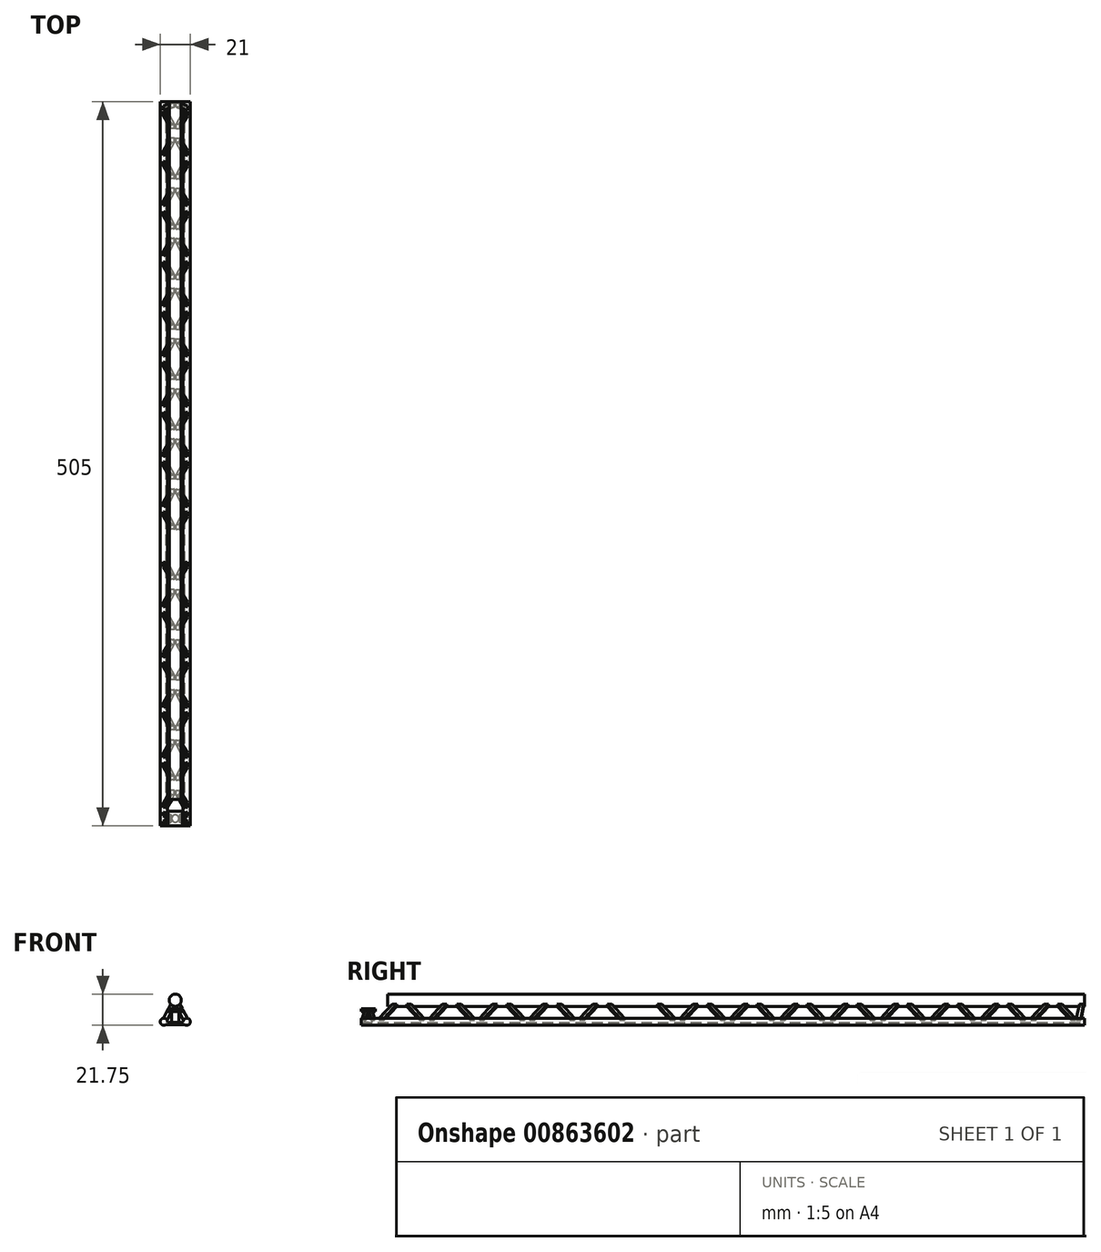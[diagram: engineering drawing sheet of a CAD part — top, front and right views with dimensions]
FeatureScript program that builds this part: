
annotation { "Feature Type Name" : "Feature", "Feature Type Description" : "" }
export const myFeature = defineFeature(function(context is Context, id is Id, definition is map)
    precondition{}
    {
        {
            var Q0;
            Q0=qCreatedBy(makeId("Front.planeOp"),FACE);
            var sketch = newSketch(context, id + "F0", { "sketchPlane" : qUnion([Q0])});
            skCircle(sketch, "E0", {"center": v(0, 15) * mm, "radius": 4.25 * mm});
            skCircle(sketch, "E1", {"center": v(8, 0) * mm, "radius": 2.5 * mm});
            skCircle(sketch, "E2", {"center": v(-8, 0) * mm, "radius": 2.5 * mm});
            skPoint(sketch, "E3.orphan", {"position": v(5, 0) * mm});
            skPoint(sketch, "E4.trimOffspring.end.orphan", {"position": v(6.27, -0.5) * mm});
            skPoint(sketch, "E5.start.orphan", {"position": v(8, -0.5) * mm});
            skPoint(sketch, "E6.start.orphan", {"position": v(-8, -0.5) * mm});
            skLineSegment(sketch, "E7", {"start": v(8, -0.5) * mm, "end": v(-8, -0.5) * mm});
            skLineSegment(sketch, "E8", {"start": v(-8, -0.5) * mm, "end": v(-8, -2) * mm});
            skLineSegment(sketch, "E9", {"start": v(8, -2) * mm, "end": v(8, -0.5) * mm});
            skLineSegment(sketch, "E10", {"start": v(-8, -2) * mm, "end": v(8, -2) * mm});
            skLineSegment(sketch, "E11.trimOffspring", {"start": v(-2, 11.25) * mm, "end": v(0, 15) * mm});
            skLineSegment(sketch, "E12.trimOffspring", {"start": v(2, 11.25) * mm, "end": v(0, 15) * mm});
            skPoint(sketch, "E13.start.orphan", {"position": v(-8, 0.5) * mm});
            skSolve(sketch);
        }
        {
            var Q0;
            {var subQ0=sQuery(id+"F0.wireOp",EDGE,"LZUzRoGq-g3zI-HQgy-fxkl-23XwhQn27evI");var subQ1=sQuery(id+"F0.wireOp",EDGE,"E1");var subQ2=makeQuery(id+"F0.imprint","INTERSECT",VERTEX,{"derivedFrom":[subQ1,subQ0]});Q0=makeQuery(id+"F0.imprint","IMPRINT",FACE,{"disambiguationData":[TD([[makeQuery(id+"F0.imprint","IMPRINT",EDGE,{"disambiguationData":[TD([[subQ2,1.0]])],"derivedFrom":subQ1}),1.0]])]});}
            var Q1;
            {var subQ0=sQuery(id+"F0.wireOp",EDGE,"E13");var subQ1=sQuery(id+"F0.wireOp",EDGE,"E2");var subQ2=makeQuery(id+"F0.imprint","INTERSECT",VERTEX,{"derivedFrom":[subQ1,subQ0]});Q1=makeQuery(id+"F0.imprint","IMPRINT",FACE,{"disambiguationData":[TD([[makeQuery(id+"F0.imprint","IMPRINT",EDGE,{"disambiguationData":[TD([[subQ2,-1.0]])],"derivedFrom":subQ1}),1.0]])]});}
            var Q2;
            {var subQ0=sQuery(id+"F0.wireOp",EDGE,"E13");var subQ1=sQuery(id+"F0.wireOp",EDGE,"E0");var subQ2=makeQuery(id+"F0.imprint","INTERSECT",VERTEX,{"derivedFrom":[subQ1,subQ0]});Q2=makeQuery(id+"F0.imprint","IMPRINT",FACE,{"disambiguationData":[TD([[makeQuery(id+"F0.imprint","IMPRINT",EDGE,{"disambiguationData":[TD([[subQ2,-1.0]])],"derivedFrom":subQ1}),1.0]])]});}
            var Q3;
            {var subQ0=sQuery(id+"F0.wireOp",EDGE,"LZUzRoGq-g3zI-HQgy-fxkl-23XwhQn27evI");var subQ1=sQuery(id+"F0.wireOp",EDGE,"E1");var subQ2=makeQuery(id+"F0.imprint","INTERSECT",VERTEX,{"derivedFrom":[subQ1,subQ0]});Q3=makeQuery(id+"F0.imprint","IMPRINT",FACE,{"disambiguationData":[TD([[makeQuery(id+"F0.imprint","IMPRINT",EDGE,{"disambiguationData":[TD([[subQ2,-1.0]])],"derivedFrom":subQ1}),1.0]])]});}
            var Q4;
            {var subQ0=sQuery(id+"F0.wireOp",EDGE,"E13");var subQ1=sQuery(id+"F0.wireOp",EDGE,"E2");var subQ2=makeQuery(id+"F0.imprint","INTERSECT",VERTEX,{"derivedFrom":[subQ1,subQ0]});Q4=makeQuery(id+"F0.imprint","IMPRINT",FACE,{"disambiguationData":[TD([[makeQuery(id+"F0.imprint","IMPRINT",EDGE,{"disambiguationData":[TD([[subQ2,1.0]])],"derivedFrom":subQ1}),1.0]])]});}
            var Q5;
            {var subQ0=sQuery(id+"F0.wireOp",EDGE,"E13");var subQ1=sQuery(id+"F0.wireOp",EDGE,"E0");var subQ2=makeQuery(id+"F0.imprint","INTERSECT",VERTEX,{"derivedFrom":[subQ1,subQ0]});Q5=makeQuery(id+"F0.imprint","IMPRINT",FACE,{"disambiguationData":[TD([[makeQuery(id+"F0.imprint","IMPRINT",EDGE,{"disambiguationData":[TD([[subQ2,1.0]])],"derivedFrom":subQ1}),1.0]])]});}
            var Q6;
            {var subQ0=sQuery(id+"F0.wireOp",EDGE,"E7");var subQ1=sQuery(id+"F0.wireOp",EDGE,"E1");var subQ2=makeQuery(id+"F0.imprint","INTERSECT",VERTEX,{"derivedFrom":[subQ1,subQ0]});Q6=makeQuery(id+"F0.imprint","IMPRINT",FACE,{"disambiguationData":[TD([[makeQuery(id+"F0.imprint","IMPRINT",EDGE,{"disambiguationData":[TD([[subQ2,-1.0]])],"derivedFrom":subQ1}),-1.0]])]});}
            extrude(context, id + "F1", {"entities" : qUnion([Q0, Q1, Q2, Q3, Q4, Q5, Q6]), "depth" : 505 * mm, "offsetDistance" : 25 * mm});
        }
        {
            var Q0;
            Q0=makeQuery(id+"F1.opExtrude","SWEPT_FACE",FACE,{"disambiguationData":[OSD([sQuery(id+"F0.wireOp",EDGE,"E0")])]});
            var Q1;
            Q1=makeQuery(id+"F1.opExtrude","SWEPT_FACE",FACE,{"disambiguationData":[OSD([sQuery(id+"F0.wireOp",EDGE,"E2")])]});
            cPlane(context, id + "F2", {"entities" : qUnion([Q0, Q1]), "cplaneType" : CPlaneType.LINE_ANGLE, "offset" : 25 * mm, "angle" : 0 * degree, "width" : 150 * mm, "height" : 150 * mm});
        }
        {
            var Q0;
            Q0=qCreatedBy(id+"F2.planeOp",FACE);
            var sketch = newSketch(context, id + "F3", { "sketchPlane" : qUnion([Q0])});
            skLineSegment(sketch, "E14", {"start": v(0, -3.92) * mm, "end": v(505, -3.92) * mm});
            skLineSegment(sketch, "E15", {"start": v(0, 13.08) * mm, "end": v(505, 13.08) * mm});
            skLineSegment(sketch, "E16", {"start": v(22, -3.92) * mm, "end": v(22, 13.08) * mm});
            skLineSegment(sketch, "E17", {"start": v(39.5, 13.08) * mm, "end": v(39.5, -3.92) * mm});
            skLineSegment(sketch, "E18", {"start": v(57, 13.08) * mm, "end": v(57, -3.92) * mm});
            skLineSegment(sketch, "E19", {"start": v(74.5, 13.08) * mm, "end": v(74.5, -3.92) * mm});
            skLineSegment(sketch, "E20", {"start": v(92, 13.08) * mm, "end": v(92, -3.92) * mm});
            skLineSegment(sketch, "E21", {"start": v(109.5, 13.08) * mm, "end": v(109.5, -3.92) * mm});
            skLineSegment(sketch, "E22", {"start": v(127, 13.08) * mm, "end": v(127, -3.92) * mm});
            skLineSegment(sketch, "E23", {"start": v(144.5, 13.08) * mm, "end": v(144.5, -3.92) * mm});
            skLineSegment(sketch, "E24", {"start": v(162, 13.08) * mm, "end": v(162, -3.92) * mm});
            skLineSegment(sketch, "E25", {"start": v(179.5, 13.08) * mm, "end": v(179.5, -3.92) * mm});
            skLineSegment(sketch, "E26", {"start": v(197, 13.08) * mm, "end": v(197, -3.92) * mm});
            skLineSegment(sketch, "E27", {"start": v(214.5, 13.08) * mm, "end": v(214.5, -3.92) * mm});
            skLineSegment(sketch, "E28", {"start": v(232, 13.08) * mm, "end": v(232, -3.92) * mm});
            skLineSegment(sketch, "E29", {"start": v(8, -3.92) * mm, "end": v(22, 13.08) * mm});
            skLineSegment(sketch, "E30", {"start": v(8, -3.92) * mm, "end": v(4.76, -3.92) * mm});
            skLineSegment(sketch, "E31", {"start": v(4.76, -3.92) * mm, "end": v(18.76, 13.08) * mm});
            skLineSegment(sketch, "E32", {"start": v(18.76, 13.08) * mm, "end": v(22, 13.08) * mm});
            skLineSegment(sketch, "E33.MirrorCS", {"start": v(36, -3.92) * mm, "end": v(22, 13.08) * mm});
            skLineSegment(sketch, "E34.MirrorCS", {"start": v(39.24, -3.92) * mm, "end": v(25.24, 13.08) * mm});
            skLineSegment(sketch, "E35.MirrorCS", {"start": v(36, -3.92) * mm, "end": v(39.24, -3.92) * mm});
            skLineSegment(sketch, "E36.MirrorCS", {"start": v(25.24, 13.08) * mm, "end": v(22, 13.08) * mm});
            skLineSegment(sketch, "E37.MirrorCS", {"start": v(39.76, -3.92) * mm, "end": v(53.76, 13.08) * mm});
            skLineSegment(sketch, "E38.MirrorCS", {"start": v(43, -3.92) * mm, "end": v(57, 13.08) * mm});
            skLineSegment(sketch, "E39.MirrorCS", {"start": v(71, -3.92) * mm, "end": v(57, 13.08) * mm});
            skLineSegment(sketch, "E40.MirrorCS", {"start": v(74.24, -3.92) * mm, "end": v(60.24, 13.08) * mm});
            skLineSegment(sketch, "E41.MirrorCS", {"start": v(74.76, -3.92) * mm, "end": v(88.76, 13.08) * mm});
            skLineSegment(sketch, "E42.MirrorCS", {"start": v(78, -3.92) * mm, "end": v(92, 13.08) * mm});
            skLineSegment(sketch, "E43.MirrorCS", {"start": v(106, -3.92) * mm, "end": v(92, 13.08) * mm});
            skLineSegment(sketch, "E44.MirrorCS", {"start": v(109.24, -3.92) * mm, "end": v(95.24, 13.08) * mm});
            skLineSegment(sketch, "E45.MirrorCS", {"start": v(109.76, -3.92) * mm, "end": v(123.76, 13.08) * mm});
            skLineSegment(sketch, "E46.MirrorCS", {"start": v(113, -3.92) * mm, "end": v(127, 13.08) * mm});
            skLineSegment(sketch, "E47.MirrorCS", {"start": v(141, -3.92) * mm, "end": v(127, 13.08) * mm});
            skLineSegment(sketch, "E48.MirrorCS", {"start": v(144.24, -3.92) * mm, "end": v(130.24, 13.08) * mm});
            skLineSegment(sketch, "E49.MirrorCS", {"start": v(144.76, -3.92) * mm, "end": v(158.76, 13.08) * mm});
            skLineSegment(sketch, "E50.MirrorCS", {"start": v(148, -3.92) * mm, "end": v(162, 13.08) * mm});
            skLineSegment(sketch, "E51.MirrorCS", {"start": v(176, -3.92) * mm, "end": v(162, 13.08) * mm});
            skLineSegment(sketch, "E52.MirrorCS", {"start": v(179.24, -3.92) * mm, "end": v(165.24, 13.08) * mm});
            skLineSegment(sketch, "E53.MirrorCS", {"start": v(179.76, -3.92) * mm, "end": v(193.76, 13.08) * mm});
            skLineSegment(sketch, "E54.MirrorCS", {"start": v(183, -3.92) * mm, "end": v(197, 13.08) * mm});
            skLineSegment(sketch, "E55.MirrorCS", {"start": v(211, -3.92) * mm, "end": v(197, 13.08) * mm});
            skLineSegment(sketch, "E56.MirrorCS", {"start": v(214.24, -3.92) * mm, "end": v(200.24, 13.08) * mm});
            skLineSegment(sketch, "E57.MirrorCS", {"start": v(214.76, -3.92) * mm, "end": v(228.76, 13.08) * mm});
            skLineSegment(sketch, "E58.MirrorCS", {"start": v(218, -3.92) * mm, "end": v(232, 13.08) * mm});
            skLineSegment(sketch, "E59.MirrorCS", {"start": v(246, -3.92) * mm, "end": v(232, 13.08) * mm});
            skLineSegment(sketch, "E60.MirrorCS", {"start": v(249.24, -3.92) * mm, "end": v(235.24, 13.08) * mm});
            skLineSegment(sketch, "E61", {"start": v(249.24, -3.92) * mm, "end": v(249.24, 13.08) * mm});
            skLineSegment(sketch, "E62", {"start": v(266.74, 13.08) * mm, "end": v(266.74, -3.92) * mm});
            skLineSegment(sketch, "E63", {"start": v(284.24, 13.08) * mm, "end": v(284.24, -3.92) * mm});
            skLineSegment(sketch, "E64", {"start": v(301.74, 13.08) * mm, "end": v(301.74, -3.92) * mm});
            skLineSegment(sketch, "E65", {"start": v(319.24, 13.08) * mm, "end": v(319.24, -3.92) * mm});
            skLineSegment(sketch, "E66", {"start": v(336.74, 13.08) * mm, "end": v(336.74, -3.92) * mm});
            skLineSegment(sketch, "E67", {"start": v(354.24, 13.08) * mm, "end": v(354.24, -3.92) * mm});
            skLineSegment(sketch, "E68", {"start": v(371.74, 13.08) * mm, "end": v(371.74, -3.92) * mm});
            skLineSegment(sketch, "E69", {"start": v(389.24, 13.08) * mm, "end": v(389.24, -3.92) * mm});
            skLineSegment(sketch, "E70", {"start": v(406.74, 13.08) * mm, "end": v(406.74, -3.92) * mm});
            skLineSegment(sketch, "E71", {"start": v(424.24, 13.08) * mm, "end": v(424.24, -3.92) * mm});
            skLineSegment(sketch, "E72", {"start": v(441.74, 13.08) * mm, "end": v(441.74, -3.92) * mm});
            skLineSegment(sketch, "E73", {"start": v(459.24, 13.08) * mm, "end": v(459.24, -3.92) * mm});
            skLineSegment(sketch, "E74", {"start": v(476.74, 13.08) * mm, "end": v(476.74, -3.92) * mm});
            skLineSegment(sketch, "E75.MirrorCS", {"start": v(249.24, -3.92) * mm, "end": v(263.24, 13.08) * mm});
            skLineSegment(sketch, "E76.MirrorCS", {"start": v(252.48, -3.92) * mm, "end": v(266.48, 13.08) * mm});
            skLineSegment(sketch, "E77.MirrorCS", {"start": v(281, -3.92) * mm, "end": v(267, 13.08) * mm});
            skLineSegment(sketch, "E78.MirrorCS", {"start": v(284.24, -3.92) * mm, "end": v(270.24, 13.08) * mm});
            skLineSegment(sketch, "E79.MirrorCS", {"start": v(284.24, -3.92) * mm, "end": v(298.24, 13.08) * mm});
            skLineSegment(sketch, "E80.MirrorCS", {"start": v(287.48, -3.92) * mm, "end": v(301.48, 13.08) * mm});
            skLineSegment(sketch, "E81.MirrorCS", {"start": v(316, -3.92) * mm, "end": v(302, 13.08) * mm});
            skLineSegment(sketch, "E82.MirrorCS", {"start": v(319.24, -3.92) * mm, "end": v(305.24, 13.08) * mm});
            skLineSegment(sketch, "E83.MirrorCS", {"start": v(319.24, -3.92) * mm, "end": v(333.24, 13.08) * mm});
            skLineSegment(sketch, "E84.MirrorCS", {"start": v(322.48, -3.92) * mm, "end": v(336.48, 13.08) * mm});
            skLineSegment(sketch, "E85.MirrorCS", {"start": v(351, -3.92) * mm, "end": v(337, 13.08) * mm});
            skLineSegment(sketch, "E86.MirrorCS", {"start": v(354.24, -3.92) * mm, "end": v(340.24, 13.08) * mm});
            skLineSegment(sketch, "E87.MirrorCS", {"start": v(354.24, -3.92) * mm, "end": v(368.24, 13.08) * mm});
            skLineSegment(sketch, "E88.MirrorCS", {"start": v(357.48, -3.92) * mm, "end": v(371.48, 13.08) * mm});
            skLineSegment(sketch, "E89.MirrorCS", {"start": v(386, -3.92) * mm, "end": v(372, 13.08) * mm});
            skLineSegment(sketch, "E90.MirrorCS", {"start": v(389.24, -3.92) * mm, "end": v(375.24, 13.08) * mm});
            skLineSegment(sketch, "E91.MirrorCS", {"start": v(389.24, -3.92) * mm, "end": v(403.24, 13.08) * mm});
            skLineSegment(sketch, "E92.MirrorCS", {"start": v(392.48, -3.92) * mm, "end": v(406.48, 13.08) * mm});
            skLineSegment(sketch, "E93.MirrorCS", {"start": v(421, -3.92) * mm, "end": v(407, 13.08) * mm});
            skLineSegment(sketch, "E94.MirrorCS", {"start": v(424.24, -3.92) * mm, "end": v(410.24, 13.08) * mm});
            skLineSegment(sketch, "E95.MirrorCS", {"start": v(424.24, -3.92) * mm, "end": v(438.24, 13.08) * mm});
            skLineSegment(sketch, "E96.MirrorCS", {"start": v(427.48, -3.92) * mm, "end": v(441.48, 13.08) * mm});
            skLineSegment(sketch, "E97.MirrorCS", {"start": v(456, -3.92) * mm, "end": v(442, 13.08) * mm});
            skLineSegment(sketch, "E98.MirrorCS", {"start": v(459.24, -3.92) * mm, "end": v(445.24, 13.08) * mm});
            skLineSegment(sketch, "E99.MirrorCS", {"start": v(459.24, -3.92) * mm, "end": v(473.24, 13.08) * mm});
            skLineSegment(sketch, "E100.MirrorCS", {"start": v(462.48, -3.92) * mm, "end": v(476.48, 13.08) * mm});
            skPoint(sketch, "E101.orphan", {"position": v(3.05, 13.08) * mm});
            skLineSegment(sketch, "E102", {"start": v(0, 13.08) * mm, "end": v(3.05, -3.92) * mm});
            skLineSegment(sketch, "E103", {"start": v(3.05, 13.08) * mm, "end": v(6.38, -3.92) * mm});
            skLineSegment(sketch, "E104", {"start": v(495, 13.08) * mm, "end": v(495, -3.92) * mm});
            skLineSegment(sketch, "E105.MirrorCS", {"start": v(491, -3.92) * mm, "end": v(477, 13.08) * mm});
            skLineSegment(sketch, "E106.MirrorCS", {"start": v(494.24, -3.92) * mm, "end": v(480.24, 13.08) * mm});
            skLineSegment(sketch, "E107.MirrorCS", {"start": v(953.48, 13.08) * mm, "end": v(448.48, 13.08) * mm});
            skLineSegment(sketch, "E108", {"start": v(495, -3.92) * mm, "end": v(497.5, 4.58) * mm});
            skPoint(sketch, "E109.orphan", {"position": v(458.48, 13.08) * mm});
            skPoint(sketch, "E110.MirrorCS.end.orphan", {"position": v(458.48, -3.92) * mm});
            skPoint(sketch, "E111.start.orphan", {"position": v(497.5, -3.92) * mm});
            skLineSegment(sketch, "E112", {"start": v(500, 13.08) * mm, "end": v(500, -3.92) * mm});
            skLineSegment(sketch, "E113", {"start": v(497.5, -3.92) * mm, "end": v(499.7, 3.58) * mm});
            skPoint(sketch, "E114.end.orphan", {"position": v(500, 4.58) * mm});
            skLineSegment(sketch, "E115", {"start": v(497.5, 4.58) * mm, "end": v(502.5, 4.58) * mm});
            skLineSegment(sketch, "E116", {"start": v(499.7, 3.58) * mm, "end": v(500.14, 3.58) * mm});
            skPoint(sketch, "E117.MirrorCS.start.orphan", {"position": v(502.5, -3.92) * mm});
            skLineSegment(sketch, "E118.MirrorCS", {"start": v(502.5, -3.92) * mm, "end": v(500.3, 3.58) * mm});
            skLineSegment(sketch, "E119.MirrorCS", {"start": v(505, -3.92) * mm, "end": v(502.5, 4.58) * mm});
            skLineSegment(sketch, "E120", {"start": v(500.14, 3.58) * mm, "end": v(500.3, 3.58) * mm});
            skSolve(sketch);
        }
        {
            var Q0;
            {var subQ0=sQuery(id+"F3.wireOp",EDGE,"E59.MirrorCS");Q0=makeQuery(id+"F3.imprint","IMPRINT",FACE,{"disambiguationData":[TD([[makeQuery(id+"F3.imprint","IMPRINT",EDGE,{"derivedFrom":subQ0}),-1.0]])]});}
            var Q1;
            Q1=makeQuery(id+"F3.imprint","IMPRINT",FACE,{"disambiguationData":[TD([[makeQuery(id+"F3.imprint","IMPRINT",EDGE,{"derivedFrom":sQuery(id+"F3.wireOp",EDGE,"E29")}),1.0]])]});
            var Q2;
            {var subQ0=sQuery(id+"F3.wireOp",EDGE,"E37.MirrorCS");Q2=makeQuery(id+"F3.imprint","IMPRINT",FACE,{"disambiguationData":[TD([[makeQuery(id+"F3.imprint","IMPRINT",EDGE,{"derivedFrom":subQ0}),-1.0]])]});}
            var Q3;
            {var subQ2=sQuery(id+"F3.wireOp",EDGE,"E39.MirrorCS");Q3=makeQuery(id+"F3.imprint","IMPRINT",FACE,{"disambiguationData":[TD([[makeQuery(id+"F3.imprint","IMPRINT",EDGE,{"derivedFrom":subQ2}),-1.0]])]});}
            var Q4;
            {var subQ2=sQuery(id+"F3.wireOp",EDGE,"E42.MirrorCS");Q4=makeQuery(id+"F3.imprint","IMPRINT",FACE,{"disambiguationData":[TD([[makeQuery(id+"F3.imprint","IMPRINT",EDGE,{"derivedFrom":subQ2}),1.0]])]});}
            var Q5;
            {var subQ2=sQuery(id+"F3.wireOp",EDGE,"E43.MirrorCS");Q5=makeQuery(id+"F3.imprint","IMPRINT",FACE,{"disambiguationData":[TD([[makeQuery(id+"F3.imprint","IMPRINT",EDGE,{"derivedFrom":subQ2}),-1.0]])]});}
            var Q6;
            {var subQ0=sQuery(id+"F3.wireOp",EDGE,"E45.MirrorCS");Q6=makeQuery(id+"F3.imprint","IMPRINT",FACE,{"disambiguationData":[TD([[makeQuery(id+"F3.imprint","IMPRINT",EDGE,{"derivedFrom":subQ0}),-1.0]])]});}
            var Q7;
            {var subQ2=sQuery(id+"F3.wireOp",EDGE,"E47.MirrorCS");Q7=makeQuery(id+"F3.imprint","IMPRINT",FACE,{"disambiguationData":[TD([[makeQuery(id+"F3.imprint","IMPRINT",EDGE,{"derivedFrom":subQ2}),-1.0]])]});}
            var Q8;
            {var subQ0=sQuery(id+"F3.wireOp",EDGE,"E49.MirrorCS");Q8=makeQuery(id+"F3.imprint","IMPRINT",FACE,{"disambiguationData":[TD([[makeQuery(id+"F3.imprint","IMPRINT",EDGE,{"derivedFrom":subQ0}),-1.0]])]});}
            var Q9;
            {var subQ2=sQuery(id+"F3.wireOp",EDGE,"E51.MirrorCS");Q9=makeQuery(id+"F3.imprint","IMPRINT",FACE,{"disambiguationData":[TD([[makeQuery(id+"F3.imprint","IMPRINT",EDGE,{"derivedFrom":subQ2}),-1.0]])]});}
            var Q10;
            {var subQ0=sQuery(id+"F3.wireOp",EDGE,"E53.MirrorCS");Q10=makeQuery(id+"F3.imprint","IMPRINT",FACE,{"disambiguationData":[TD([[makeQuery(id+"F3.imprint","IMPRINT",EDGE,{"derivedFrom":subQ0}),-1.0]])]});}
            var Q11;
            {var subQ2=sQuery(id+"F3.wireOp",EDGE,"E55.MirrorCS");Q11=makeQuery(id+"F3.imprint","IMPRINT",FACE,{"disambiguationData":[TD([[makeQuery(id+"F3.imprint","IMPRINT",EDGE,{"derivedFrom":subQ2}),-1.0]])]});}
            var Q12;
            {var subQ0=sQuery(id+"F3.wireOp",EDGE,"E57.MirrorCS");Q12=makeQuery(id+"F3.imprint","IMPRINT",FACE,{"disambiguationData":[TD([[makeQuery(id+"F3.imprint","IMPRINT",EDGE,{"derivedFrom":subQ0}),-1.0]])]});}
            var Q13;
            Q13=makeQuery(id+"F3.imprint","IMPRINT",FACE,{"disambiguationData":[TD([[makeQuery(id+"F3.imprint","IMPRINT",EDGE,{"derivedFrom":sQuery(id+"F3.wireOp",EDGE,"E33.MirrorCS")}),-1.0]])]});
            var Q14;
            {var subQ0=sQuery(id+"F3.wireOp",EDGE,"E75.MirrorCS");Q14=makeQuery(id+"F3.imprint","IMPRINT",FACE,{"disambiguationData":[TD([[makeQuery(id+"F3.imprint","IMPRINT",EDGE,{"derivedFrom":subQ0}),-1.0]])]});}
            var Q15;
            {var subQ2=sQuery(id+"F3.wireOp",EDGE,"E77.MirrorCS");Q15=makeQuery(id+"F3.imprint","IMPRINT",FACE,{"disambiguationData":[TD([[makeQuery(id+"F3.imprint","IMPRINT",EDGE,{"derivedFrom":subQ2}),-1.0]])]});}
            var Q16;
            {var subQ0=sQuery(id+"F3.wireOp",EDGE,"E79.MirrorCS");Q16=makeQuery(id+"F3.imprint","IMPRINT",FACE,{"disambiguationData":[TD([[makeQuery(id+"F3.imprint","IMPRINT",EDGE,{"derivedFrom":subQ0}),-1.0]])]});}
            var Q17;
            {var subQ2=sQuery(id+"F3.wireOp",EDGE,"E81.MirrorCS");Q17=makeQuery(id+"F3.imprint","IMPRINT",FACE,{"disambiguationData":[TD([[makeQuery(id+"F3.imprint","IMPRINT",EDGE,{"derivedFrom":subQ2}),-1.0]])]});}
            var Q18;
            {var subQ0=sQuery(id+"F3.wireOp",EDGE,"E83.MirrorCS");Q18=makeQuery(id+"F3.imprint","IMPRINT",FACE,{"disambiguationData":[TD([[makeQuery(id+"F3.imprint","IMPRINT",EDGE,{"derivedFrom":subQ0}),-1.0]])]});}
            var Q19;
            {var subQ2=sQuery(id+"F3.wireOp",EDGE,"E85.MirrorCS");Q19=makeQuery(id+"F3.imprint","IMPRINT",FACE,{"disambiguationData":[TD([[makeQuery(id+"F3.imprint","IMPRINT",EDGE,{"derivedFrom":subQ2}),-1.0]])]});}
            var Q20;
            {var subQ0=sQuery(id+"F3.wireOp",EDGE,"E87.MirrorCS");Q20=makeQuery(id+"F3.imprint","IMPRINT",FACE,{"disambiguationData":[TD([[makeQuery(id+"F3.imprint","IMPRINT",EDGE,{"derivedFrom":subQ0}),-1.0]])]});}
            var Q21;
            {var subQ2=sQuery(id+"F3.wireOp",EDGE,"E89.MirrorCS");Q21=makeQuery(id+"F3.imprint","IMPRINT",FACE,{"disambiguationData":[TD([[makeQuery(id+"F3.imprint","IMPRINT",EDGE,{"derivedFrom":subQ2}),-1.0]])]});}
            var Q22;
            {var subQ0=sQuery(id+"F3.wireOp",EDGE,"E91.MirrorCS");Q22=makeQuery(id+"F3.imprint","IMPRINT",FACE,{"disambiguationData":[TD([[makeQuery(id+"F3.imprint","IMPRINT",EDGE,{"derivedFrom":subQ0}),-1.0]])]});}
            var Q23;
            {var subQ2=sQuery(id+"F3.wireOp",EDGE,"E93.MirrorCS");Q23=makeQuery(id+"F3.imprint","IMPRINT",FACE,{"disambiguationData":[TD([[makeQuery(id+"F3.imprint","IMPRINT",EDGE,{"derivedFrom":subQ2}),-1.0]])]});}
            var Q24;
            {var subQ0=sQuery(id+"F3.wireOp",EDGE,"E95.MirrorCS");Q24=makeQuery(id+"F3.imprint","IMPRINT",FACE,{"disambiguationData":[TD([[makeQuery(id+"F3.imprint","IMPRINT",EDGE,{"derivedFrom":subQ0}),-1.0]])]});}
            var Q25;
            {var subQ2=sQuery(id+"F3.wireOp",EDGE,"E97.MirrorCS");Q25=makeQuery(id+"F3.imprint","IMPRINT",FACE,{"disambiguationData":[TD([[makeQuery(id+"F3.imprint","IMPRINT",EDGE,{"derivedFrom":subQ2}),-1.0]])]});}
            var Q26;
            {var subQ0=sQuery(id+"F3.wireOp",EDGE,"E99.MirrorCS");Q26=makeQuery(id+"F3.imprint","IMPRINT",FACE,{"disambiguationData":[TD([[makeQuery(id+"F3.imprint","IMPRINT",EDGE,{"derivedFrom":subQ0}),-1.0]])]});}
            var Q27;
            {var subQ0=sQuery(id+"F3.wireOp",EDGE,"E102");Q27=makeQuery(id+"F3.imprint","IMPRINT",FACE,{"disambiguationData":[TD([[makeQuery(id+"F3.imprint","IMPRINT",EDGE,{"derivedFrom":subQ0}),1.0]])]});}
            var Q28;
            {var subQ2=sQuery(id+"F3.wireOp",EDGE,"E100.MirrorCS");Q28=makeQuery(id+"F3.imprint","IMPRINT",FACE,{"disambiguationData":[TD([[makeQuery(id+"F3.imprint","IMPRINT",EDGE,{"derivedFrom":subQ2}),1.0]])]});}
            var Q29;
            {var subQ0=sQuery(id+"F3.wireOp",EDGE,"E105.MirrorCS");Q29=makeQuery(id+"F3.imprint","IMPRINT",FACE,{"disambiguationData":[TD([[makeQuery(id+"F3.imprint","IMPRINT",EDGE,{"derivedFrom":subQ0}),-1.0]])]});}
            var Q30;
            {var subQ6=sQuery(id+"F3.wireOp",EDGE,"E108");Q30=makeQuery(id+"F3.imprint","IMPRINT",FACE,{"disambiguationData":[TD([[makeQuery(id+"F3.imprint","IMPRINT",EDGE,{"derivedFrom":subQ6}),-1.0]])]});}
            var Q31;
            {var subQ0=sQuery(id+"F3.wireOp",EDGE,"E118.MirrorCS");Q31=makeQuery(id+"F3.imprint","IMPRINT",FACE,{"disambiguationData":[TD([[makeQuery(id+"F3.imprint","IMPRINT",EDGE,{"derivedFrom":subQ0}),-1.0]])]});}
            extrude(context, id + "F4", {"entities" : qUnion([Q0, Q1, Q2, Q3, Q4, Q5, Q6, Q7, Q8, Q9, Q10, Q11, Q12, Q13, Q14, Q15, Q16, Q17, Q18, Q19, Q20, Q21, Q22, Q23, Q24, Q25, Q26, Q27, Q28, Q29, Q30, Q31]), "operationType" : NewBodyOperationType.ADD, "endBound" : BoundingType.SYMMETRIC, "depth" : 3 * mm, "offsetDistance" : 25 * mm});
        }
        {
            var Q0;
            Q0=makeQuery(id+"F1.opExtrude","SWEPT_BODY",BODY,{"disambiguationData":[OSD([sQuery(id+"F0.wireOp",EDGE,"E0")])]});
            var Q1;
            Q1=qCreatedBy(makeId("Right.planeOp"),FACE);
            mirror(context, id + "F5", {"entities" : qUnion([Q0]), "mirrorPlane" : qUnion([Q1])});
        }
        {
            var Q0;
            Q0=makeQuery(id+"F1.opExtrude","CAP_FACE",FACE,{"disambiguationData":[OSD([sQuery(id+"F0.wireOp",EDGE,"E0")])],"isStart":false});
            var sketch = newSketch(context, id + "F6", { "sketchPlane" : qUnion([Q0])});
            skLineSegment(sketch, "E121", {"start": v(0, 7) * mm, "end": v(-5, 7) * mm});
            skLineSegment(sketch, "E122", {"start": v(-5, 7) * mm, "end": v(0, 7) * mm});
            skLineSegment(sketch, "E123", {"start": v(0, 7) * mm, "end": v(5, 7) * mm});
            skLineSegment(sketch, "E124", {"start": v(-5, 7) * mm, "end": v(-5, 9) * mm});
            skLineSegment(sketch, "E125", {"start": v(-5, 9) * mm, "end": v(5, 9) * mm});
            skLineSegment(sketch, "E126", {"start": v(5, 9) * mm, "end": v(5, 7) * mm});
            skPoint(sketch, "E127.start.orphan", {"position": v(-7.98, 0) * mm});
            skSolve(sketch);
        }
        {
            var Q0;
            Q0 = qSketchRegion(id + "F6", true);
            extrude(context, id + "F7", {"entities" : qUnion([Q0]), "oppositeDirection" : true, "depth" : 10 * mm, "offsetDistance" : 25 * mm});
        }
        {
            var Q0;
            Q0=qCreatedBy(makeId("Right.planeOp"),FACE);
            var sketch = newSketch(context, id + "F8", { "sketchPlane" : qUnion([Q0])});
            skLineSegment(sketch, "E128", {"start": v(-486.6, 19.52) * mm, "end": v(-486.6, 10.14) * mm});
            skLineSegment(sketch, "E129", {"start": v(-508.6, 10.14) * mm, "end": v(-508.6, 19.52) * mm});
            skLineSegment(sketch, "E130", {"start": v(-508.6, 19.52) * mm, "end": v(-486.6, 19.52) * mm});
            skLineSegment(sketch, "E131", {"start": v(-486.6, 10.14) * mm, "end": v(-508.6, 10.14) * mm});
            skSolve(sketch);
        }
        {
            var Q0;
            Q0 = qSketchRegion(id + "F8", true);
            extrude(context, id + "F9", {"entities" : qUnion([Q0]), "operationType" : NewBodyOperationType.REMOVE, "endBound" : BoundingType.SYMMETRIC, "depth" : 25 * mm, "offsetDistance" : 25 * mm});
        }
        {
            var Q0;
            Q0=makeQuery(id+"F7.opExtrude","SWEPT_FACE",FACE,{"disambiguationData":[OSD([sQuery(id+"F6.wireOp",EDGE,"E125")])]});
            var sketch = newSketch(context, id + "F10", { "sketchPlane" : qUnion([Q0])});
            skCircle(sketch, "E132", {"center": v(0, -500) * mm, "radius": 2.5 * mm});
            skPoint(sketch, "E132.centerSnap0", {"position": v(-5, -500) * mm});
            skPoint(sketch, "E132.centerSnap1", {"position": v(0, -505) * mm});
            skSolve(sketch);
        }
        {
            var Q0;
            Q0 = qSketchRegion(id + "F10", true);
            extrude(context, id + "F11", {"entities" : qUnion([Q0]), "operationType" : NewBodyOperationType.ADD, "oppositeDirection" : true, "depth" : 10.5 * mm, "offsetDistance" : 25 * mm});
        }
    });
